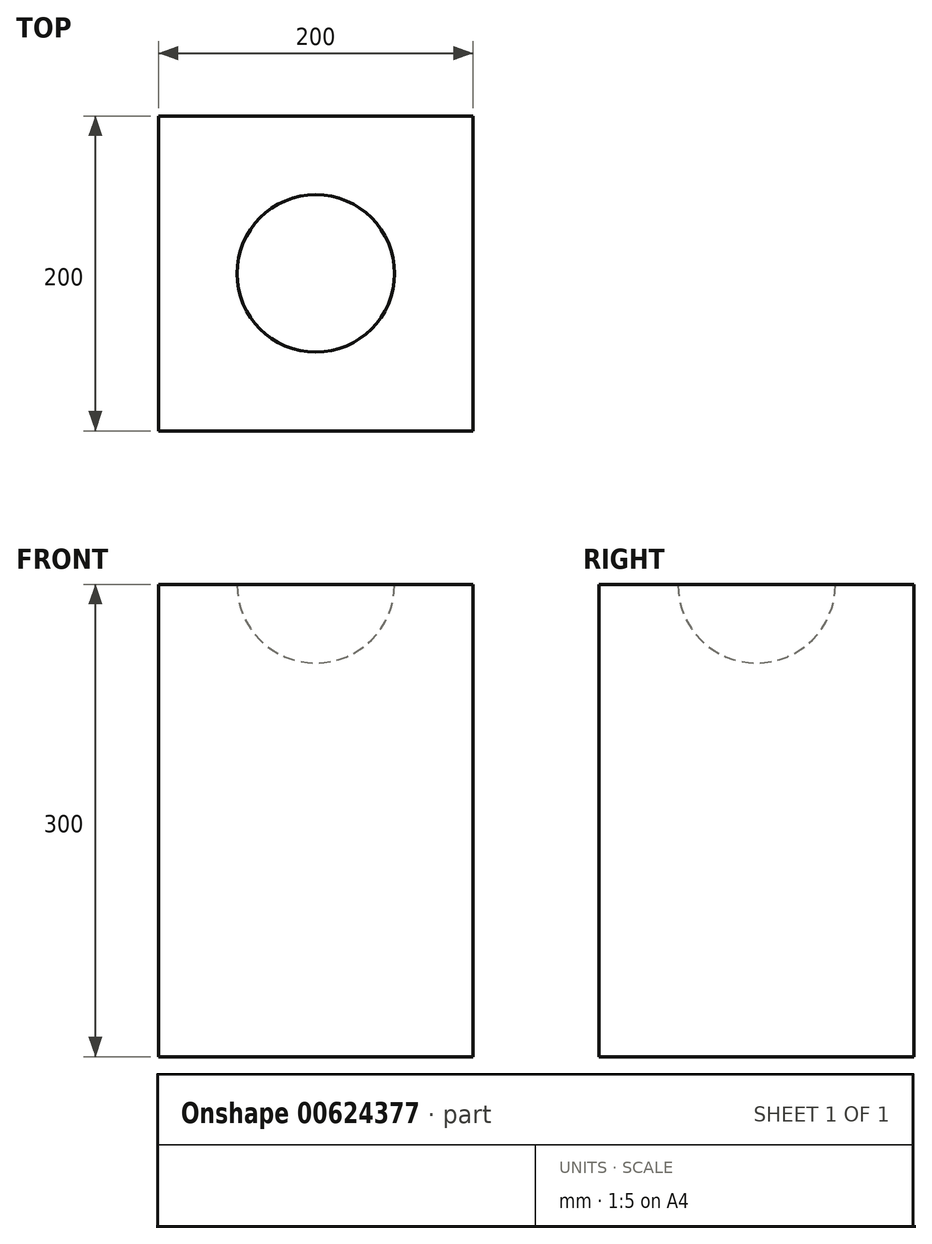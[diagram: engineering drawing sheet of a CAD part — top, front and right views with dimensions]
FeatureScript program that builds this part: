
annotation { "Feature Type Name" : "Feature", "Feature Type Description" : "" }
export const myFeature = defineFeature(function(context is Context, id is Id, definition is map)
    precondition{}
    {
        {
            var Q0;
            Q0=qCreatedBy(makeId("Top.planeOp"),FACE);
            var sketch = newSketch(context, id + "F0", { "sketchPlane" : qUnion([Q0])});
            skLineSegment(sketch, "E0.bottom", {"start": v(100, -100) * mm, "end": v(-100, -100) * mm});
            skLineSegment(sketch, "E0.top", {"start": v(100, 100) * mm, "end": v(-100, 100) * mm});
            skLineSegment(sketch, "E0.left", {"start": v(100, -100) * mm, "end": v(100, 100) * mm});
            skLineSegment(sketch, "E0.right", {"start": v(-100, -100) * mm, "end": v(-100, 100) * mm});
            skPoint(sketch, "E0.middle", {"position": v(0, 0) * mm});
            skSolve(sketch);
        }
        {
            var Q0;
            Q0=makeQuery(id+"F0.imprint","IMPRINT",FACE,{"disambiguationData":[TD([[makeQuery(id+"F0.imprint","IMPRINT",EDGE,{"derivedFrom":sQuery(id+"F0.wireOp",EDGE,"E0.bottom")}),-1.0]])]});
            extrude(context, id + "F1", {"entities" : qUnion([Q0]), "depth" : 300 * mm, "offsetDistance" : 25 * mm});
        }
        {
            var Q0;
            Q0=qCreatedBy(makeId("Right.planeOp"),FACE);
            var sketch = newSketch(context, id + "F2", { "sketchPlane" : qUnion([Q0])});
            skLineSegment(sketch, "E1.0", {"start": v(-100, 300) * mm, "end": v(100, 300) * mm});
            skArc(sketch, "E2", {"start": v(50, 300) * mm, "mid": v(0, 350) * mm, "end": v(-50, 300) * mm});
            skSolve(sketch);
        }
        {
            var Q0;
            Q0 = qSketchRegion(id + "F2", true);
            var Q1;
            Q1=sQuery(id+"F2.wireOp",EDGE,"E1.0");
            revolve(context, id + "F3", {"operationType" : NewBodyOperationType.REMOVE, "entities" : qUnion([Q0]), "axis" : qUnion([Q1]), "revolveType" : RevolveType.FULL, "oppositeDirection" : true});
        }
    });
